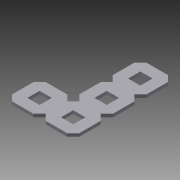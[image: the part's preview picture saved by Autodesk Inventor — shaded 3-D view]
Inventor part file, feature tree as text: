
AUTODESK INVENTOR PART (.ipt)
format: ipt  version: 2012 (Build 160160000, 160)  size: 1,946,112 bytes
history: native  units: in
note: dims shown in document units (in); Inventor stores cm internally (conversion verified against a paired STEP export)
features: sketch x3, other x1, imported_body x1, plane x1, split x1, extrude x1
ambient origin geometry x8: Origin, YZ Plane, XZ Plane, XY Plane, X Axis, Y Axis, Z Axis, Center Point
feature tree (8):
  parser-record x1  (decoder bookkeeping rows leaked as tree rows — omitted from the tree; the rows remain in map.json)
  imported_body  "Base1"
  sketch  "Sketch2"  dims[d6=9.8425in d8=0.5in d9=1.9685in d11=0.5in d16=-2.5in]
  plane  "Work Plane1"
  split  "Split1"
  sketch  "Sketch4"  dims[d17=1.0in d18=0.0in]
  extrude  "Extrusion2"  [1 undecoded]
  sketch  "Sketch5"
note: 1 required parameter value undecoded (feature->parameter linkage not recoverable at this tier; creation-order binding heuristic only, values carry confidence <= 0.55)
